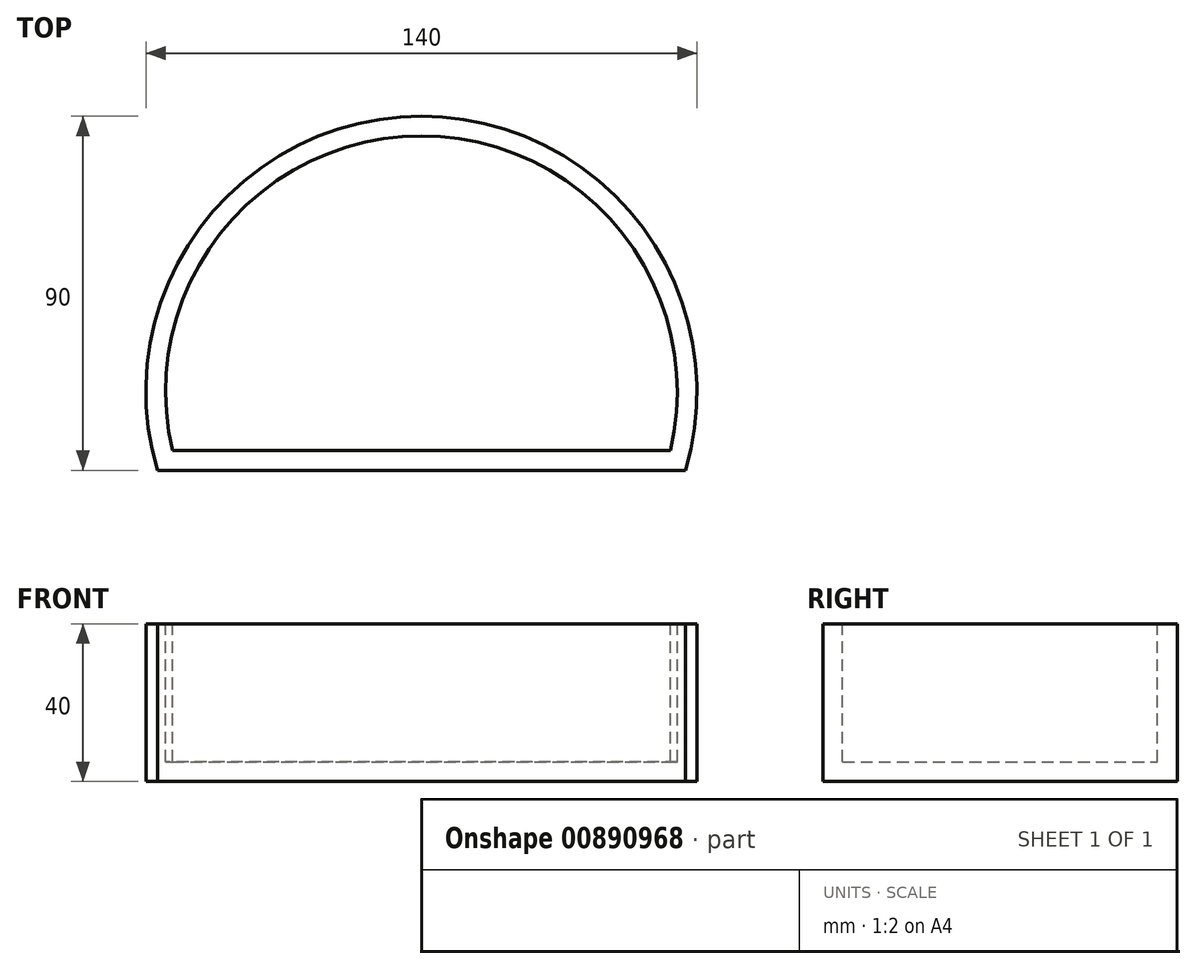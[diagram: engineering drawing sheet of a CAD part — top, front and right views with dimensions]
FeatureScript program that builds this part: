
annotation { "Feature Type Name" : "Feature", "Feature Type Description" : "" }
export const myFeature = defineFeature(function(context is Context, id is Id, definition is map)
    precondition{}
    {
        {
            var Q0;
            Q0=qCreatedBy(makeId("Top.planeOp"),FACE);
            var sketch = newSketch(context, id + "F0", { "sketchPlane" : qUnion([Q0])});
            skArc(sketch, "E0", {"start": v(67.08, -20) * mm, "mid": v(0, 70) * mm, "end": v(-67.08, -20) * mm});
            skLineSegment(sketch, "E1", {"start": v(-67.08, -20) * mm, "end": v(67.08, -20) * mm});
            skSolve(sketch);
        }
        {
            var Q0;
            Q0 = qSketchRegion(id + "F0", true);
            extrude(context, id + "F1", {"entities" : qUnion([Q0]), "oppositeDirection" : true, "depth" : 40 * mm, "offsetDistance" : 25 * mm});
        }
        {
            var Q0;
            Q0=makeQuery(id+"F1.opExtrude","CAP_FACE",FACE,{"disambiguationData":[OSD([sQuery(id+"F0.wireOp",EDGE,"E0"),sQuery(id+"F0.wireOp",EDGE,"E1")])],"isStart":true});
            var sketch = newSketch(context, id + "F2", { "sketchPlane" : qUnion([Q0])});
            skArc(sketch, "E2", {"start": v(63.25, -15) * mm, "mid": v(0, 65) * mm, "end": v(-63.25, -15) * mm});
            skLineSegment(sketch, "E3", {"start": v(-63.25, -15) * mm, "end": v(63.25, -15) * mm});
            skSolve(sketch);
        }
        {
            var Q0;
            Q0 = qSketchRegion(id + "F2", true);
            extrude(context, id + "F3", {"entities" : qUnion([Q0]), "operationType" : NewBodyOperationType.REMOVE, "oppositeDirection" : true, "depth" : 35 * mm, "offsetDistance" : 25 * mm});
        }
    });
